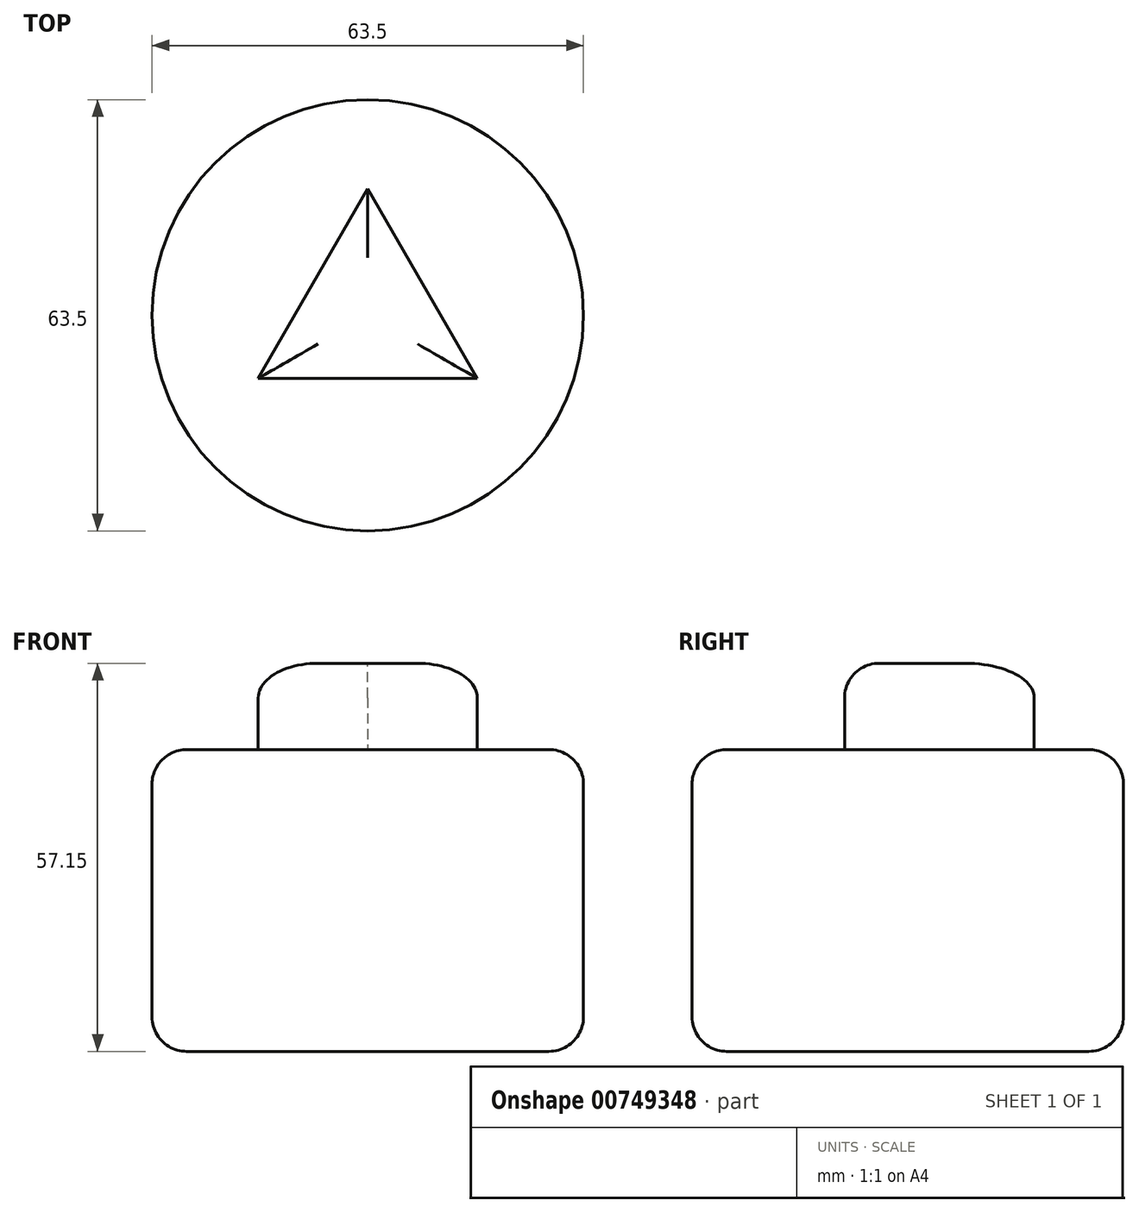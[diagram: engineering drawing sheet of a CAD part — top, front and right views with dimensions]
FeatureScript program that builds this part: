
annotation { "Feature Type Name" : "Feature", "Feature Type Description" : "" }
export const myFeature = defineFeature(function(context is Context, id is Id, definition is map)
    precondition{}
    {
        {
            var Q0;
            Q0=qCreatedBy(makeId("Top.planeOp"),FACE);
            var sketch = newSketch(context, id + "F0", { "sketchPlane" : qUnion([Q0])});
            skCircle(sketch, "E0", {"center": v(0, 0) * mm, "radius": 31.75 * mm});
            skSolve(sketch);
        }
        {
            var Q0;
            Q0=makeQuery(id+"F0.imprint","IMPRINT",FACE,{"disambiguationData":[TD([[makeQuery(id+"F0.imprint","IMPRINT",EDGE,{"derivedFrom":sQuery(id+"F0.wireOp",EDGE,"E0")}),1.0]])]});
            extrude(context, id + "F1", {"entities" : qUnion([Q0]), "depth" : 44.45 * mm, "offsetDistance" : 25.4 * mm});
        }
        {
            var Q0;
            Q0=makeQuery(id+"F1.opExtrude","CAP_FACE",FACE,{"disambiguationData":[OSD([sQuery(id+"F0.wireOp",EDGE,"E0")])],"isStart":false});
            var sketch = newSketch(context, id + "F2", { "sketchPlane" : qUnion([Q0])});
            skCircle(sketch, "E1.cCircle", {"center": v(0, 0) * mm, "radius": 9.3 * mm, "construction": true});
            skLineSegment(sketch, "E1.0", {"start": v(16.13, -9.3) * mm, "end": v(-16.13, -9.3) * mm});
            skLineSegment(sketch, "E1.1", {"start": v(-16.13, -9.3) * mm, "end": v(0, 18.62) * mm});
            skLineSegment(sketch, "E1.2", {"start": v(0, 18.62) * mm, "end": v(16.13, -9.3) * mm});
            skPoint(sketch, "E1.0.midPoint", {"position": v(0, -9.3) * mm});
            skSolve(sketch);
        }
        {
            var Q0;
            Q0=makeQuery(id+"F2.imprint","IMPRINT",FACE,{"disambiguationData":[TD([[makeQuery(id+"F2.imprint","IMPRINT",EDGE,{"derivedFrom":sQuery(id+"F2.wireOp",EDGE,"E1.0")}),-1.0]])]});
            extrude(context, id + "F3", {"entities" : qUnion([Q0]), "operationType" : NewBodyOperationType.ADD, "depth" : 12.7 * mm, "offsetDistance" : 25.4 * mm});
        }
        {
            var Q0;
            Q0=makeQuery(id+"F1.opExtrude","CAP_EDGE",EDGE,{"disambiguationData":[OSD([sQuery(id+"F0.wireOp",EDGE,"E0")])],"isStart":true});
            var Q1;
            Q1=makeQuery(id+"F1.opExtrude","CAP_EDGE",EDGE,{"disambiguationData":[OSD([sQuery(id+"F0.wireOp",EDGE,"E0")])],"isStart":false});
            var Q2;
            Q2=makeQuery(id+"F3.opExtrude","CAP_EDGE",EDGE,{"disambiguationData":[OSD([sQuery(id+"F2.wireOp",EDGE,"E1.0")])],"isStart":false});
            var Q3;
            Q3=makeQuery(id+"F3.opExtrude","CAP_EDGE",EDGE,{"disambiguationData":[OSD([sQuery(id+"F2.wireOp",EDGE,"E1.1")])],"isStart":false});
            var Q4;
            Q4=makeQuery(id+"F3.opExtrude","CAP_EDGE",EDGE,{"disambiguationData":[OSD([sQuery(id+"F2.wireOp",EDGE,"E1.2")])],"isStart":false});
            fillet(context, id + "F4", {"entities" : qUnion([Q0, Q1, Q2, Q3, Q4]), "radius" : 5.08 * mm, "tangentPropagation" : true, "allowEdgeOverflow" : false});
        }
    });
